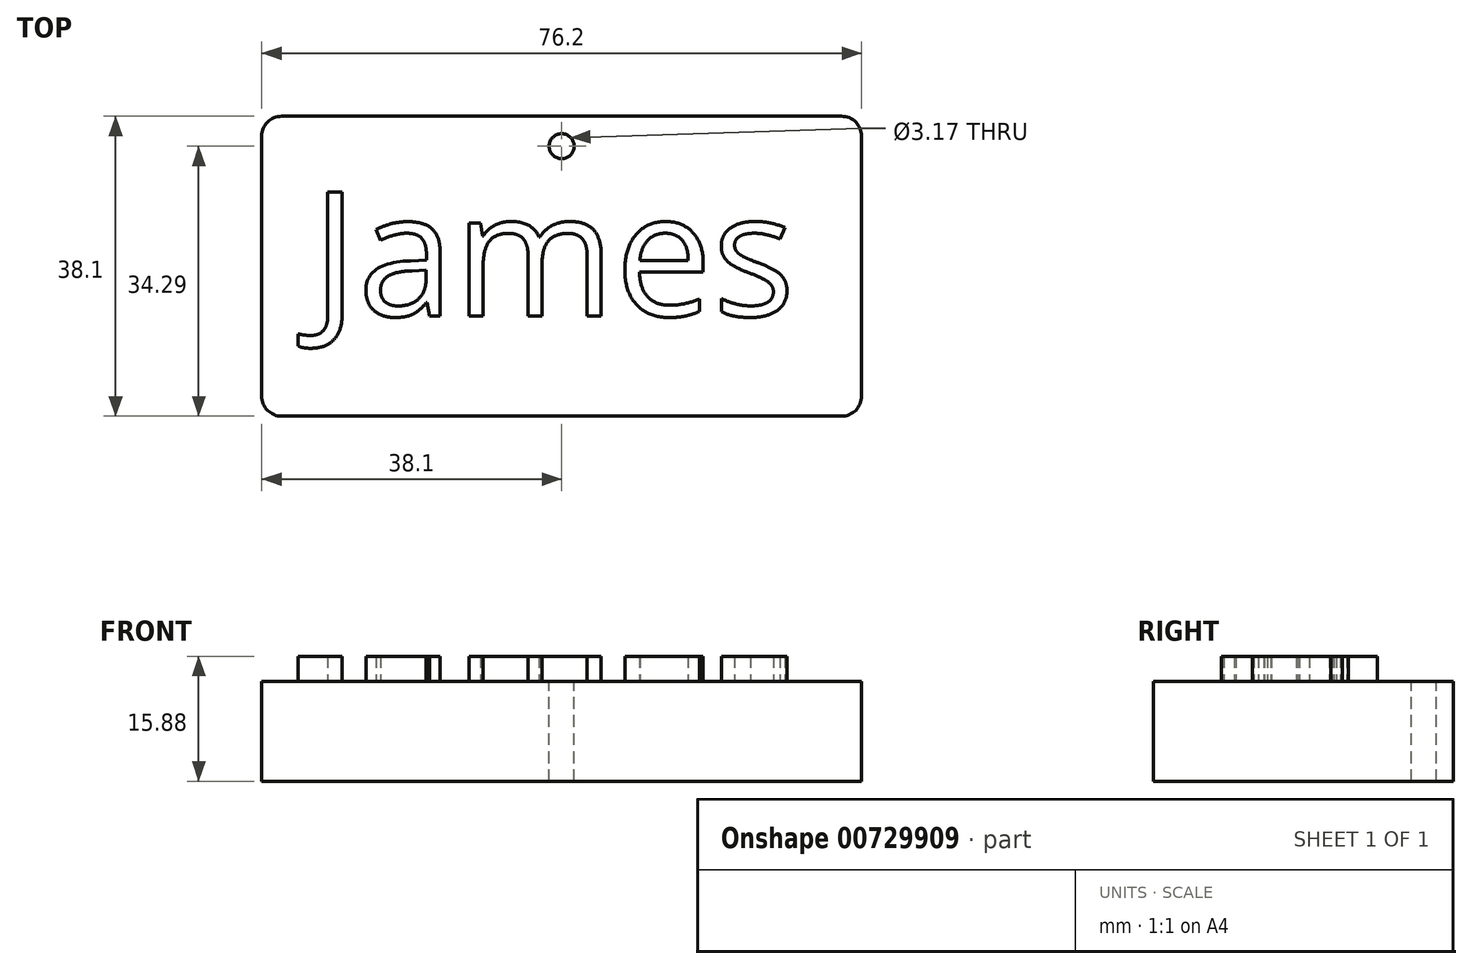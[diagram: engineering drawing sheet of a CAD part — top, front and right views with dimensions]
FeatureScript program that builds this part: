
annotation { "Feature Type Name" : "Feature", "Feature Type Description" : "" }
export const myFeature = defineFeature(function(context is Context, id is Id, definition is map)
    precondition{}
    {
        {
            var Q0;
            Q0=qCreatedBy(makeId("Top.planeOp"),FACE);
            var sketch = newSketch(context, id + "F0", { "sketchPlane" : qUnion([Q0])});
            skLineSegment(sketch, "E0.bottom", {"start": v(38.1, 19.05) * mm, "end": v(-38.1, 19.05) * mm});
            skLineSegment(sketch, "E0.top", {"start": v(38.1, -19.05) * mm, "end": v(-38.1, -19.05) * mm});
            skLineSegment(sketch, "E0.left", {"start": v(38.1, 19.05) * mm, "end": v(38.1, -19.05) * mm});
            skLineSegment(sketch, "E0.right", {"start": v(-38.1, 19.05) * mm, "end": v(-38.1, -19.05) * mm});
            skPoint(sketch, "E0.middle", {"position": v(0, 0) * mm});
            skSolve(sketch);
        }
        {
            var Q0;
            Q0=makeQuery(id+"F0.imprint","IMPRINT",FACE,{"disambiguationData":[TD([[makeQuery(id+"F0.imprint","IMPRINT",EDGE,{"derivedFrom":sQuery(id+"F0.wireOp",EDGE,"E0.bottom")}),1.0]])]});
            extrude(context, id + "F1", {"entities" : qUnion([Q0]), "depth" : 12.7 * mm, "offsetDistance" : 25.4 * mm});
        }
        {
            var Q0;
            Q0=makeQuery(id+"F1.opExtrude","CAP_FACE",FACE,{"disambiguationData":[OSD([sQuery(id+"F0.wireOp",EDGE,"E0.bottom"),sQuery(id+"F0.wireOp",EDGE,"E0.top"),sQuery(id+"F0.wireOp",EDGE,"E0.left"),sQuery(id+"F0.wireOp",EDGE,"E0.right")])],"isStart":false});
            var sketch = newSketch(context, id + "F2", { "sketchPlane" : qUnion([Q0])});
            skText(sketch, "E1", { "text": "James", "fontName": "OpenSans-Regular.ttf"});
            const initialGuessF2  = {"E1": [-0.03175, -0.0063, 1, 0, 0.01583]};
            skSetInitialGuess(sketch, initialGuessF2);
            skSolve(sketch);
        }
        {
            var Q0;
            Q0 = qSketchRegion(id + "F2", true);
            extrude(context, id + "F3", {"entities" : qUnion([Q0]), "operationType" : NewBodyOperationType.ADD, "depth" : 3.17 * mm, "offsetDistance" : 25.4 * mm});
        }
        {
            var Q0;
            {var subQ0=sQuery(id+"F0.wireOp",EDGE,"E0.top");var subQ1=sQuery(id+"F0.wireOp",EDGE,"E0.right");var subQ2=sQuery(id+"F0.wireOp",EDGE,"E0.bottom");var subQ3=sQuery(id+"F0.wireOp",EDGE,"E0.left");Q0=makeQuery(id+"F3.boolean.opBoolean","SPLIT",FACE,{"disambiguationData":[TD([makeQuery(id+"F1.opExtrude","SWEPT_FACE",FACE,{"disambiguationData":[OSD([subQ2])]})])],"derivedFrom":makeQuery(id+"F1.opExtrude","CAP_FACE",FACE,{"disambiguationData":[OSD([subQ2,subQ0,subQ3,subQ1])],"isStart":false})});}
            var sketch = newSketch(context, id + "F4", { "sketchPlane" : qUnion([Q0])});
            skCircle(sketch, "E2", {"center": v(0, 15.24) * mm, "radius": 1.59 * mm});
            skLineSegment(sketch, "E3", {"start": v(0, 15.24) * mm, "end": v(0, 19.05) * mm, "construction": true});
            skSolve(sketch);
        }
        {
            var Q0;
            Q0=makeQuery(id+"F4.imprint","IMPRINT",FACE,{"disambiguationData":[TD([[makeQuery(id+"F4.imprint","IMPRINT",EDGE,{"derivedFrom":sQuery(id+"F4.wireOp",EDGE,"E2")}),1.0]])]});
            extrude(context, id + "F5", {"entities" : qUnion([Q0]), "operationType" : NewBodyOperationType.REMOVE, "oppositeDirection" : true, "depth" : 25.4 * mm, "offsetDistance" : 25.4 * mm});
        }
        {
            var Q0;
            Q0=makeQuery(id+"F1.opExtrude","SWEPT_EDGE",EDGE,{"disambiguationData":[OSD([sQuery(id+"F0.wireOp",EDGE,"E0.bottom"),sQuery(id+"F0.wireOp",EDGE,"E0.left")])]});
            var Q1;
            Q1=makeQuery(id+"F1.opExtrude","SWEPT_EDGE",EDGE,{"disambiguationData":[OSD([sQuery(id+"F0.wireOp",EDGE,"E0.bottom"),sQuery(id+"F0.wireOp",EDGE,"E0.right")])]});
            var Q2;
            Q2=makeQuery(id+"F1.opExtrude","SWEPT_EDGE",EDGE,{"disambiguationData":[OSD([sQuery(id+"F0.wireOp",EDGE,"E0.top"),sQuery(id+"F0.wireOp",EDGE,"E0.right")])]});
            var Q3;
            Q3=makeQuery(id+"F1.opExtrude","SWEPT_EDGE",EDGE,{"disambiguationData":[OSD([sQuery(id+"F0.wireOp",EDGE,"E0.top"),sQuery(id+"F0.wireOp",EDGE,"E0.left")])]});
            fillet(context, id + "F6", {"entities" : qUnion([Q0, Q1, Q2, Q3]), "radius" : 2.54 * mm, "tangentPropagation" : true, "allowEdgeOverflow" : false});
        }
    });
